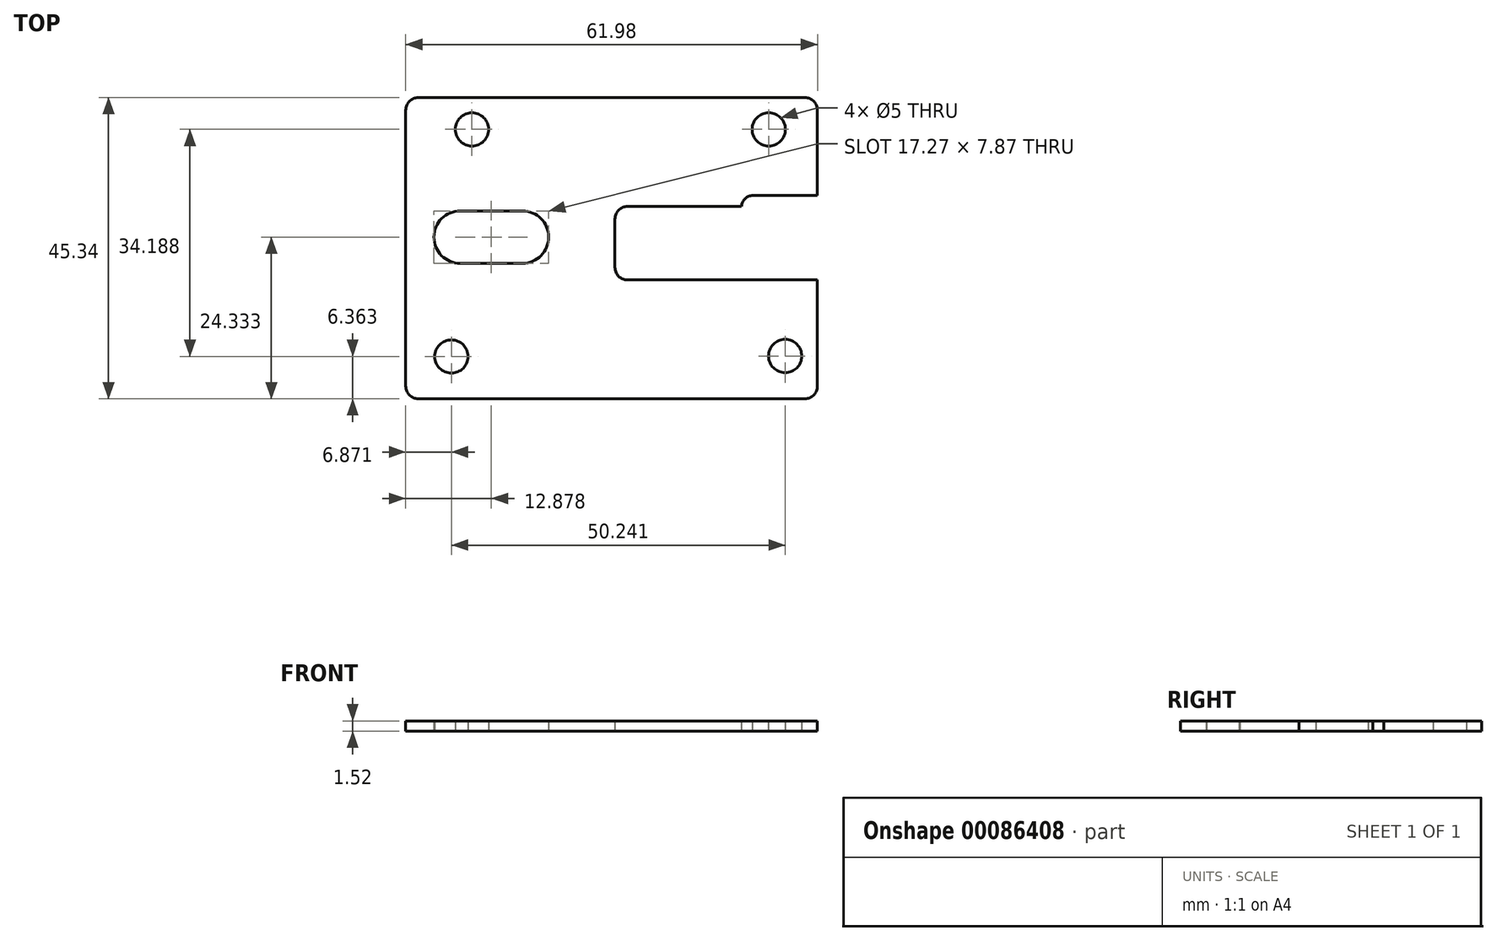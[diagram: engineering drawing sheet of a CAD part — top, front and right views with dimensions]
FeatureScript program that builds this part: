
annotation { "Feature Type Name" : "Feature", "Feature Type Description" : "" }
export const myFeature = defineFeature(function(context is Context, id is Id, definition is map)
    precondition{}
    {
        {
            var Q0;
            Q0=qCreatedBy(makeId("Top.planeOp"),FACE);
            var sketch = newSketch(context, id + "F0", { "sketchPlane" : qUnion([Q0])});
            skLineSegment(sketch, "E0.bottom", {"start": v(0, 0) * mm, "end": v(61.98, 0) * mm});
            skLineSegment(sketch, "E0.top", {"start": v(0, 45.34) * mm, "end": v(61.98, 45.34) * mm});
            skLineSegment(sketch, "E0.left", {"start": v(0, 0) * mm, "end": v(0, 45.34) * mm});
            skLineSegment(sketch, "E0.right", {"start": v(61.98, 0) * mm, "end": v(61.98, 45.34) * mm});
            skLineSegment(sketch, "E1", {"start": v(12.88, 45.34) * mm, "end": v(12.88, 28.27) * mm, "construction": true});
            skLineSegment(sketch, "E2", {"start": v(12.88, 28.27) * mm, "end": v(12.88, 20.4) * mm, "construction": true});
            skLineSegment(sketch, "E3", {"start": v(12.88, 24.33) * mm, "end": v(21.51, 24.33) * mm, "construction": true});
            skLineSegment(sketch, "E4", {"start": v(12.88, 24.33) * mm, "end": v(4.24, 24.33) * mm, "construction": true});
            skCircle(sketch, "E5", {"center": v(17.58, 24.33) * mm, "radius": 3.94 * mm, "construction": true});
            skLineSegment(sketch, "E6", {"start": v(12.88, 28.27) * mm, "end": v(17.58, 28.27) * mm});
            skLineSegment(sketch, "E7", {"start": v(12.88, 28.27) * mm, "end": v(8.18, 28.27) * mm});
            skCircle(sketch, "E8", {"center": v(8.18, 24.33) * mm, "radius": 3.94 * mm, "construction": true});
            skLineSegment(sketch, "E9", {"start": v(8.18, 20.4) * mm, "end": v(17.58, 20.4) * mm});
            skArc(sketch, "E10", {"start": v(8.18, 28.27) * mm, "mid": v(4.24, 24.33) * mm, "end": v(8.18, 20.4) * mm});
            skArc(sketch, "E11", {"start": v(17.58, 20.4) * mm, "mid": v(21.51, 24.33) * mm, "end": v(17.58, 28.27) * mm});
            skCircle(sketch, "E12", {"center": v(9.97, 40.55) * mm, "radius": 2.5 * mm});
            skCircle(sketch, "E13", {"center": v(54.65, 40.55) * mm, "radius": 2.5 * mm});
            skCircle(sketch, "E14", {"center": v(6.87, 6.36) * mm, "radius": 2.5 * mm});
            skCircle(sketch, "E15", {"center": v(57.11, 6.44) * mm, "radius": 2.5 * mm});
            skLineSegment(sketch, "E16", {"start": v(61.98, 17.88) * mm, "end": v(31.5, 17.88) * mm});
            skLineSegment(sketch, "E17", {"start": v(31.5, 17.88) * mm, "end": v(31.5, 28.96) * mm});
            skLineSegment(sketch, "E18", {"start": v(31.5, 28.96) * mm, "end": v(61.98, 28.96) * mm, "construction": true});
            skLineSegment(sketch, "E19", {"start": v(61.98, 30.6) * mm, "end": v(50.55, 30.6) * mm, "construction": true});
            skLineSegment(sketch, "E20", {"start": v(50.55, 30.6) * mm, "end": v(50.55, 28.96) * mm, "construction": true});
            skLineSegment(sketch, "E21", {"start": v(31.5, 28.96) * mm, "end": v(50.55, 28.96) * mm});
            skCircle(sketch, "E22", {"center": v(52.28, 28.87) * mm, "radius": 1.74 * mm, "construction": true});
            skArc(sketch, "E23", {"start": v(52.28, 30.6) * mm, "mid": v(51.08, 30.13) * mm, "end": v(50.55, 28.96) * mm});
            skLineSegment(sketch, "E24", {"start": v(52.28, 30.6) * mm, "end": v(61.98, 30.6) * mm});
            skSolve(sketch);
        }
        {
            var Q0;
            {var subQ0=sQuery(id+"F0.wireOp",EDGE,"E0.bottom");Q0=makeQuery(id+"F0.imprint","IMPRINT",FACE,{"disambiguationData":[TD([[makeQuery(id+"F0.imprint","IMPRINT",EDGE,{"derivedFrom":subQ0}),1.0]])]});}
            extrude(context, id + "F1", {"entities" : qUnion([Q0]), "depth" : 1.52 * mm});
        }
        {
            var Q0;
            Q0=makeQuery(id+"F1.opExtrude","SWEPT_EDGE",EDGE,{"disambiguationData":[OSD([sQuery(id+"F0.wireOp",EDGE,"E17"),sQuery(id+"F0.wireOp",EDGE,"E21")])]});
            var Q1;
            Q1=makeQuery(id+"F1.opExtrude","SWEPT_EDGE",EDGE,{"disambiguationData":[OSD([sQuery(id+"F0.wireOp",EDGE,"E16"),sQuery(id+"F0.wireOp",EDGE,"E17")])]});
            var Q2;
            Q2=makeQuery(id+"F1.opExtrude","SWEPT_EDGE",EDGE,{"disambiguationData":[OSD([sQuery(id+"F0.wireOp",EDGE,"E0.top"),sQuery(id+"F0.wireOp",EDGE,"E0.left")])]});
            var Q3;
            Q3=makeQuery(id+"F1.opExtrude","SWEPT_EDGE",EDGE,{"disambiguationData":[OSD([sQuery(id+"F0.wireOp",EDGE,"E0.bottom"),sQuery(id+"F0.wireOp",EDGE,"E0.left")])]});
            var Q4;
            Q4=makeQuery(id+"F1.opExtrude","SWEPT_EDGE",EDGE,{"disambiguationData":[OSD([sQuery(id+"F0.wireOp",EDGE,"E0.bottom"),sQuery(id+"F0.wireOp",EDGE,"E0.right")])]});
            var Q5;
            Q5=makeQuery(id+"F1.opExtrude","SWEPT_EDGE",EDGE,{"disambiguationData":[OSD([sQuery(id+"F0.wireOp",EDGE,"E0.top"),sQuery(id+"F0.wireOp",EDGE,"E0.right")])]});
            fillet(context, id + "F2", {"entities" : qUnion([Q0, Q1, Q2, Q3, Q4, Q5]), "radius" : 1.9 * mm, "tangentPropagation" : true, "allowEdgeOverflow" : false});
        }
    });
